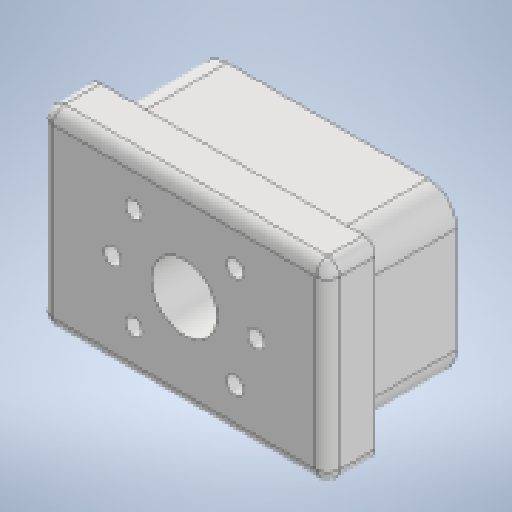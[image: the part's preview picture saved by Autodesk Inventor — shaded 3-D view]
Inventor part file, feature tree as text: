
AUTODESK INVENTOR PART (.ipt)
format: ipt  version: 2023 (Build 270158000, 158)  size: 209,920 bytes
history: native  units: in
note: dims shown in document units (in); Inventor stores cm internally (conversion verified against a paired STEP export)
features: extrude x3, sketch x3, projected_geometry x2, fillet x1, chamfer x1
ambient origin geometry x8: Origin, YZ Plane, XZ Plane, XY Plane, X Axis, Y Axis, Z Axis, Center Point
bodies: Solid1 (feature_tree)
feature tree (10):
  extrude  "Extrusion1"  Depth=1.7in
  extrude  "Extrusion2"  Depth=1.0in TaperAngle=0.0deg
  fillet  "Fillet1"  Radius=3.0in
  extrude  "Extrusion3"  Depth=0.125in
  chamfer  "Chamfer1"  Distance=0.5in
  sketch  "Sketch1"  dims[d0=2.7in d1=1.7in]
  sketch  "Sketch2"  dims[d2=0.3in d3=1.0in d4=0.0in d5=3.0in]
  sketch  "Sketch3"  dims[d6=2.0in d7=0.125in d8=0.5in d9=0.0in d10=0.125in d11=0.689in d12=0.5in d13=0.0in d14=0.1772in d15=1.4961in d16=45.0deg d17=0.05in d18=0.125in d19=45.0deg]
  projected_geometry  "Projected Loop1"
  projected_geometry  "Projected Loop2"
